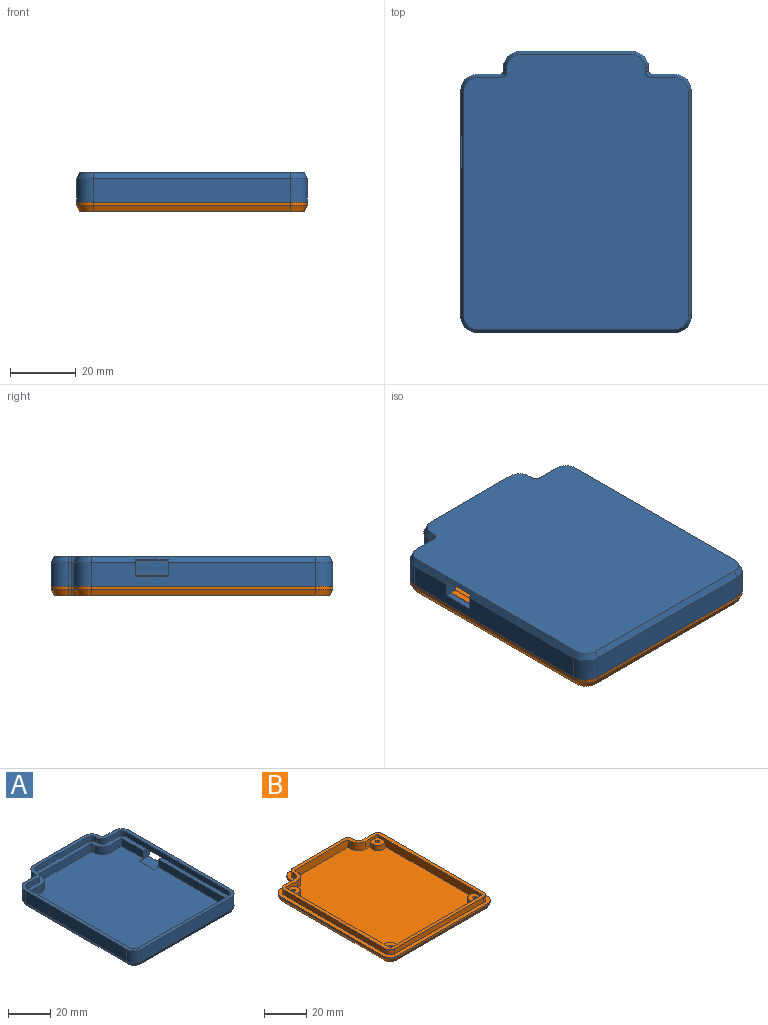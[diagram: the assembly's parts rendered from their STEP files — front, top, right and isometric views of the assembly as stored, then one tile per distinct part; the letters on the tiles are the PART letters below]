
ASSEMBLY  parts=2 mates=1
PART A: 70 faces, bbox 70x85.4x9.1 mm
  f0: plane 6.9x5mm, normal (0,-1,0), area 20.5mm2, adj f2,f3,f4,f6,f21,f51,f52,f60
  f1: plane 6.9x5mm, normal (0,1,0), area 20.5mm2, adj f3,f4,f6,f10,f21,f51,f52,f60
  f2: plane 14.5x4.6mm, normal (-1,0,0), area 66.7mm2, adj f0,f3,f4,f13
  f3: plane 81.6x66.2mm, normal (0,0,1), area 563.6mm2, adj f0,f1,f2,f7,f8,f9,f10,f11
  f4: plane 77.4x62mm, normal (0,0,1), area 4598.6mm2, adj f0,f1,f2,f7,f8,f9,f10,f11
  f5: plane 85.4x70mm, normal (0,0,1), area 550.7mm2, adj f6,f19,f20,f21,f22,f23,f24,f25
  f6: plane 68.2x7.1mm, normal (1,0,0), area 443.2mm2, adj f0,f1,f5,f36,f43,f60,f69
  f7: plane 34.2x4.6mm, normal (0,-1,0), area 157.3mm2, adj f3,f4,f17,f18
  f8: plane 70.4x4.6mm, normal (1,0,0), area 323.8mm2, adj f3,f4,f9,f14
  f9: plane 62x4.6mm, normal (0,1,0), area 285.2mm2, adj f3,f4,f8,f10
  f10: plane 45.9x4.6mm, normal (-1,0,0), area 211.1mm2, adj f1,f3,f4,f9
  f11: plane 4.6x1mm, normal (1,0,0), area 4.6mm2, adj f3,f4,f16,f18
  f12: plane 4.6x1mm, normal (-1,0,0), area 4.6mm2, adj f3,f4,f15,f17
  f13: plane 7.9x4.6mm, normal (0,-1,0), area 36.3mm2, adj f2,f3,f4,f15
  f14: plane 7.9x4.6mm, normal (0,-1,0), area 36.3mm2, adj f3,f4,f8,f16
  f15: cylinder r=5.1mm len=5.1mm, axis (0,0,1), area 36.9mm2, adj f3,f4,f12,f13
  f16: cylinder r=5.1mm len=5.1mm, axis (0,0,-1), area 36.9mm2, adj f3,f4,f11,f14
  f17: cylinder r=0.9mm len=4.6mm, axis (0,0,1), area 6.5mm2, adj f3,f4,f7,f12
  f18: cylinder r=0.9mm len=4.6mm, axis (0,0,-1), area 6.5mm2, adj f3,f4,f7,f11
  f19: plane 68.6x3.1mm, normal (1,0,0), area 212.7mm2, adj f3,f5,f33,f34
  f20: plane 60.2x3.1mm, normal (0,1,0), area 186.6mm2, adj f3,f5,f32,f33
  f21: plane 68.6x3.1mm, normal (-1,0,0), area 211.7mm2, adj f0,f1,f3,f5,f31,f32,f69
  f22: plane 7x3.1mm, normal (0,-1,0), area 21.7mm2, adj f3,f5,f23,f34
  f23: cylinder r=3mm len=3.1mm, axis (0,0,-1), area 14.6mm2, adj f3,f5,f22,f24
  f24: plane 3.1x1mm, normal (1,0,0), area 3.1mm2, adj f3,f5,f23,f25
  f25: cylinder r=3mm len=3.1mm, axis (0,0,-1), area 14.6mm2, adj f3,f5,f24,f26
  f26: plane 34.2x3.1mm, normal (0,-1,0), area 106mm2, adj f3,f5,f25,f27
  f27: cylinder r=3mm len=3.1mm, axis (0,0,-1), area 14.6mm2, adj f3,f5,f26,f28
  f28: plane 3.1x1mm, normal (-1,0,0), area 3.1mm2, adj f3,f5,f27,f29
  f29: cylinder r=3mm len=3.1mm, axis (0,0,-1), area 14.6mm2, adj f3,f5,f28,f30
  f30: plane 7x3.1mm, normal (0,-1,0), area 21.7mm2, adj f3,f5,f29,f31
  f31: cylinder r=3mm len=3.1mm, axis (0,0,-1), area 14.6mm2, adj f3,f5,f21,f30
  f32: cylinder r=3mm len=3.1mm, axis (0,0,-1), area 14.6mm2, adj f3,f5,f20,f21
  f33: cylinder r=3mm len=3.1mm, axis (0,0,-1), area 14.6mm2, adj f3,f5,f19,f20
  f34: cylinder r=3mm len=3.1mm, axis (0,0,-1), area 14.6mm2, adj f3,f5,f19,f22
  f35: plane 83.4x68mm, normal (0,0,-1), area 5469.1mm2, adj f53,f54,f55,f56,f57,f58,f59,f60
  f36: cylinder r=5.1mm len=7.1mm, axis (0,0,-1), area 56.9mm2, adj f5,f6,f42,f62
  f37: cylinder r=5.1mm len=7.1mm, axis (0,0,-1), area 56.9mm2, adj f5,f39,f41,f67
  f38: cylinder r=5.1mm len=7.1mm, axis (0,0,1), area 56.9mm2, adj f5,f39,f50,f63
  f39: plane 33.8x7.1mm, normal (0,1,0), area 240mm2, adj f5,f37,f38,f65
  f40: cylinder r=0.9mm len=7.1mm, axis (0,0,-1), area 10mm2, adj f5,f41,f42,f66
  f41: plane 7.1x1mm, normal (1,0,0), area 7.1mm2, adj f5,f37,f40,f68
  f42: plane 7.1x7mm, normal (0,1,0), area 49.7mm2, adj f5,f36,f40,f64
  f43: cylinder r=5.1mm len=7.1mm, axis (0,0,1), area 56.9mm2, adj f5,f6,f45,f58
  f44: cylinder r=5.1mm len=7.1mm, axis (0,0,-1), area 56.9mm2, adj f5,f45,f47,f54
  f45: plane 59.8x7.1mm, normal (0,-1,0), area 424.6mm2, adj f5,f43,f44,f56
  f46: cylinder r=5.1mm len=7.1mm, axis (0,0,1), area 56.9mm2, adj f5,f47,f49,f55
  f47: plane 68.2x7.1mm, normal (-1,0,0), area 484.2mm2, adj f5,f44,f46,f53
  f48: cylinder r=0.9mm len=7.1mm, axis (0,0,1), area 10mm2, adj f5,f49,f50,f59
  f49: plane 7.1x7mm, normal (0,1,0), area 49.7mm2, adj f5,f46,f48,f57
  f50: plane 7.1x1mm, normal (-1,0,0), area 7.1mm2, adj f5,f38,f48,f61
  f51: plane 10x0.3mm, normal (1,0,0), area 3mm2, adj f0,f1,f4,f52
  f52: plane 10x6.45mm, normal (0,0,1), area 64.5mm2, adj f0,f1,f51,f60
  f53: plane 68.2x2mm, normal (-0.89,0,-0.45), area 152.5mm2, adj f35,f47,f54,f55
  f54: cone r=4.1mm half-angle=26.6deg, axis (0,0,1), area 16.2mm2, adj f35,f44,f53,f56
  f55: cone r=4.1mm half-angle=26.6deg, axis (0,0,1), area 16.2mm2, adj f35,f46,f53,f57
  f56: plane 59.8x2mm, normal (0,-0.89,-0.45), area 133.7mm2, adj f35,f45,f54,f58
  f57: plane 7x2mm, normal (0,0.89,-0.45), area 15.7mm2, adj f35,f49,f55,f59
  f58: cone r=4.1mm half-angle=26.6deg, axis (0,0,1), area 16.2mm2, adj f35,f43,f56,f60
  f59: cone r=1.9mm half-angle=26.6deg, axis (0,0,-1), area 4.9mm2, adj f35,f48,f57,f61
  f60: plane 68.2x2mm, normal (0.89,0,-0.45), area 142.4mm2, adj f0,f1,f6,f35,f52,f58,f62
  f61: plane 2x1mm, normal (-0.89,0,-0.45), area 2.2mm2, adj f35,f50,f59,f63
  f62: cone r=4.1mm half-angle=26.6deg, axis (0,0,1), area 16.2mm2, adj f35,f36,f60,f64
  f63: cone r=4.1mm half-angle=26.6deg, axis (0,0,1), area 16.2mm2, adj f35,f38,f61,f65
  f64: plane 7x2mm, normal (0,0.89,-0.45), area 15.7mm2, adj f35,f42,f62,f66
  f65: plane 33.8x2mm, normal (0,0.89,-0.45), area 75.6mm2, adj f35,f39,f63,f67
  f66: cone r=1.9mm half-angle=26.6deg, axis (0,0,-1), area 4.9mm2, adj f35,f40,f64,f68
  f67: cone r=4.1mm half-angle=26.6deg, axis (0,0,1), area 16.2mm2, adj f35,f37,f65,f68
  f68: plane 2x1mm, normal (0.89,0,-0.45), area 2.2mm2, adj f35,f41,f66,f67
  f69: plane 10x1.9mm, normal (0,0,-1), area 19mm2, adj f0,f1,f6,f21
PART B: 78 faces, bbox 70x85.4x6 mm
  f0: plane 77.4x62mm, normal (0,0,1), area 4503.8mm2, adj f1,f2,f3,f4,f12,f13,f14,f15
  f1: plane 70.4x4.6mm, normal (1,0,0), area 295.6mm2, adj f0,f2,f15,f17,f28,f30,f34,f36
  f2: plane 62x4.6mm, normal (0,1,0), area 256.9mm2, adj f0,f1,f4,f17,f28,f30,f31,f33
  f3: plane 36x4.6mm, normal (0,-1,0), area 165.6mm2, adj f0,f12,f13,f17
  f4: plane 70.4x4.6mm, normal (-1,0,0), area 295.6mm2, adj f0,f2,f14,f17,f31,f33,f37,f39
  f5: plane 3x1mm, normal (-1,0,0), area 3mm2, adj f17,f26,f40,f47
  f6: plane 7x3mm, normal (0,1,0), area 21mm2, adj f17,f26,f40,f41
  f7: plane 68.2x3mm, normal (-1,0,0), area 204.6mm2, adj f17,f26,f41,f42
  f8: plane 59.8x3mm, normal (0,-1,0), area 179.4mm2, adj f17,f26,f42,f43
  f9: plane 68.2x3mm, normal (1,0,0), area 204.6mm2, adj f17,f26,f43,f44
  f10: plane 7x3mm, normal (0,1,0), area 21mm2, adj f17,f26,f44,f45
  f11: plane 3x1mm, normal (1,0,0), area 3mm2, adj f17,f26,f45,f46
  f12: plane 4.6x1.9mm, normal (1,0,0), area 8.7mm2, adj f0,f3,f17,f55
  f13: plane 4.6x1.9mm, normal (-1,0,0), area 8.7mm2, adj f0,f3,f17,f54
  f14: plane 7.9x4.6mm, normal (0,-1,0), area 22.2mm2, adj f0,f4,f17,f37,f39,f54
  f15: plane 7.9x4.6mm, normal (0,-1,0), area 22.2mm2, adj f0,f1,f17,f34,f36,f55
  f16: plane 33.8x3mm, normal (0,1,0), area 101.4mm2, adj f17,f26,f46,f47
  f17: plane 81.2x65.8mm, normal (0,0,1), area 525.3mm2, adj f1,f2,f3,f4,f5,f6,f7,f8
  f18: plane 1x1mm, normal (-1,0,0), area 1mm2, adj f26,f48,f56,f66
  f19: plane 7x1mm, normal (0,1,0), area 7mm2, adj f26,f49,f56,f62
  f20: plane 68.2x1mm, normal (-1,0,0), area 68.2mm2, adj f26,f49,f50,f58
  f21: plane 59.8x1mm, normal (0,-1,0), area 59.8mm2, adj f26,f50,f51,f61
  f22: plane 68.2x1mm, normal (1,0,0), area 68.2mm2, adj f26,f51,f52,f65
  f23: plane 7x1mm, normal (0,1,0), area 7mm2, adj f26,f52,f57,f69
  f24: plane 1x1mm, normal (1,0,0), area 1mm2, adj f26,f53,f57,f73
  f25: plane 33.8x1mm, normal (0,1,0), area 33.8mm2, adj f26,f48,f53,f70
  f26: plane 85.4x70mm, normal (0,0,1), area 609.6mm2, adj f5,f6,f7,f8,f9,f10,f11,f16
  f27: plane 83.4x68mm, normal (0,0,-1), area 5469.1mm2, adj f58,f59,f60,f61,f62,f63,f64,f65
  f28: cylinder r=3.35mm len=5.95mm, axis (0,0,-1), area 33.6mm2, adj f0,f1,f2,f30
  f29: cylinder r=0.95mm len=3.8mm, axis (0,0,-1), area 22.7mm2, adj f30,f77
  f30: plane 5.95x5.95mm, normal (0,0,1), area 28.2mm2, adj f1,f2,f28,f29
  f31: cylinder r=3.35mm len=5.95mm, axis (0,0,-1), area 33.6mm2, adj f0,f2,f4,f33
  f32: cylinder r=0.95mm len=3.8mm, axis (0,0,-1), area 22.7mm2, adj f33,f76
  f33: plane 5.95x5.95mm, normal (0,0,1), area 28.2mm2, adj f2,f4,f31,f32
  f34: cylinder r=3.35mm len=5.95mm, axis (0,0,-1), area 33.6mm2, adj f0,f1,f15,f36
  f35: cylinder r=0.95mm len=3.8mm, axis (0,0,-1), area 22.7mm2, adj f36,f75
  f36: plane 5.95x5.95mm, normal (0,0,1), area 28.2mm2, adj f1,f15,f34,f35
  f37: cylinder r=3.35mm len=5.95mm, axis (0,0,-1), area 33.6mm2, adj f0,f4,f14,f39
  f38: cylinder r=0.95mm len=3.8mm, axis (0,0,-1), area 22.7mm2, adj f39,f74
  f39: plane 5.95x5.95mm, normal (0,0,1), area 28.2mm2, adj f4,f14,f37,f38
  f40: cylinder r=3mm len=3mm, axis (0,0,1), area 14.1mm2, adj f5,f6,f17,f26
  f41: cylinder r=3mm len=3mm, axis (0,0,1), area 14.1mm2, adj f6,f7,f17,f26
  f42: cylinder r=3mm len=3mm, axis (0,0,-1), area 14.1mm2, adj f7,f8,f17,f26
  f43: cylinder r=3mm len=3mm, axis (0,0,1), area 14.1mm2, adj f8,f9,f17,f26
  f44: cylinder r=3mm len=3mm, axis (0,0,-1), area 14.1mm2, adj f9,f10,f17,f26
  f45: cylinder r=3mm len=3mm, axis (0,0,1), area 14.1mm2, adj f10,f11,f17,f26
  f46: cylinder r=3mm len=3mm, axis (0,0,-1), area 14.1mm2, adj f11,f16,f17,f26
  f47: cylinder r=3mm len=3mm, axis (0,0,-1), area 14.1mm2, adj f5,f16,f17,f26
  f48: cylinder r=5.1mm len=5.1mm, axis (0,0,1), area 8mm2, adj f18,f25,f26,f68
  f49: cylinder r=5.1mm len=5.1mm, axis (0,0,1), area 8mm2, adj f19,f20,f26,f60
  f50: cylinder r=5.1mm len=5.1mm, axis (0,0,-1), area 8mm2, adj f20,f21,f26,f59
  f51: cylinder r=5.1mm len=5.1mm, axis (0,0,1), area 8mm2, adj f21,f22,f26,f63
  f52: cylinder r=5.1mm len=5.1mm, axis (0,0,-1), area 8mm2, adj f22,f23,f26,f67
  f53: cylinder r=5.1mm len=5.1mm, axis (0,0,-1), area 8mm2, adj f24,f25,f26,f72
  f54: cylinder r=5.1mm len=5.1mm, axis (0,0,1), area 36.9mm2, adj f0,f13,f14,f17
  f55: cylinder r=5.1mm len=5.1mm, axis (0,0,-1), area 36.9mm2, adj f0,f12,f15,f17
  f56: cylinder r=0.9mm len=1mm, axis (0,0,1), area 1.4mm2, adj f18,f19,f26,f64
  f57: cylinder r=0.9mm len=1mm, axis (0,0,-1), area 1.4mm2, adj f23,f24,f26,f71
  f58: plane 68.2x2mm, normal (-0.89,0,-0.45), area 152.5mm2, adj f20,f27,f59,f60
  f59: cone r=4.1mm half-angle=26.6deg, axis (0,0,1), area 16.2mm2, adj f27,f50,f58,f61
  f60: cone r=4.1mm half-angle=26.6deg, axis (0,0,1), area 16.2mm2, adj f27,f49,f58,f62
  f61: plane 59.8x2mm, normal (0,-0.89,-0.45), area 133.7mm2, adj f21,f27,f59,f63
  f62: plane 7x2mm, normal (0,0.89,-0.45), area 15.7mm2, adj f19,f27,f60,f64
  f63: cone r=4.1mm half-angle=26.6deg, axis (0,0,1), area 16.2mm2, adj f27,f51,f61,f65
  f64: cone r=1.9mm half-angle=26.6deg, axis (0,0,-1), area 4.9mm2, adj f27,f56,f62,f66
  f65: plane 68.2x2mm, normal (0.89,0,-0.45), area 152.5mm2, adj f22,f27,f63,f67
  f66: plane 2x1mm, normal (-0.89,0,-0.45), area 2.2mm2, adj f18,f27,f64,f68
  f67: cone r=4.1mm half-angle=26.6deg, axis (0,0,1), area 16.2mm2, adj f27,f52,f65,f69
  f68: cone r=4.1mm half-angle=26.6deg, axis (0,0,1), area 16.2mm2, adj f27,f48,f66,f70
  f69: plane 7x2mm, normal (0,0.89,-0.45), area 15.7mm2, adj f23,f27,f67,f71
  f70: plane 33.8x2mm, normal (0,0.89,-0.45), area 75.6mm2, adj f25,f27,f68,f72
  f71: cone r=1.9mm half-angle=26.6deg, axis (0,0,-1), area 4.9mm2, adj f27,f57,f69,f73
  f72: cone r=4.1mm half-angle=26.6deg, axis (0,0,1), area 16.2mm2, adj f27,f53,f70,f73
  f73: plane 2x1mm, normal (0.89,0,-0.45), area 2.2mm2, adj f24,f27,f71,f72
  f74: plane 1.9x1.9mm, normal (0,0,1), area 2.8mm2, adj f38
  f75: plane 1.9x1.9mm, normal (0,0,1), area 2.8mm2, adj f35
  f76: plane 1.9x1.9mm, normal (0,0,1), area 2.8mm2, adj f32
  f77: plane 1.9x1.9mm, normal (0,0,1), area 2.8mm2, adj f29
PLACE A rot(axis=(0,1,0),180deg) t=(0,0,11.5)mm
PLACE B t=(0,0,-0.6)mm
MATE fastened A.f5 <-> B.f26  axis (0,0,-1) through (-26.4,39.2,2.4)mm
